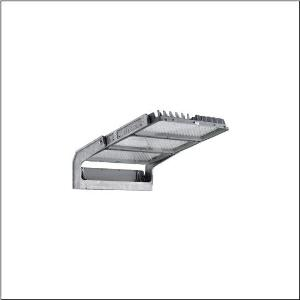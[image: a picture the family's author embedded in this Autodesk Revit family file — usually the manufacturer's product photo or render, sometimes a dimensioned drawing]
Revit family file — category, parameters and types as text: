
# Revit family: floodlight_fl_11_maxi_pro___rs07_5xa779124k01ab_afb2
name_source: partatom
category: Lighting Fixtures
units: mm (PartAtom-declared; Revit-internal decimal feet)

## family parameters
Cut with Voids When Loaded = No
Host = Face
Light Source = No
Part Type = Normal
Room Calculation Point = No
Round Connector Dimension = Use Diameter
Shared = No

## types (1)
- --- (1 x LED, 153810 lm, 1633.1 W, 5700K)
    Apparent Load = 1633 VA
    CIE Flux Codes = 80 93 99 100 99
    Color Rendering = 90
    Color Temperature = 5700K
    Default Elevation = 1800 mm
    Description = Floodlight FL 11  maxi  pro floodlight; light control with lens of PMMA; cover panel of toughened safety glass, transparent; light distribution: RS07, rotationally symmetric direct distribution, LED; colour temperature: 5700K, rated luminous flux: 153.810lm, colour rendering: CRI > 90, light colour: 957; luminous efficacy: 94lm/W; brightness control: DALI 2; with terminal, 5-pole, max. 2.5mm², mains connection: 220..240V/380..400V AC, 50/60Hz, surge voltage resistance: line to ground: 10kV, LED service life up to 100,000h L90. Typical operating time: 1000h per year., ECG replaceable separately, LED unit replaceable without ESD environment, dustproof LED module, dimming range 10..100%; 1633W floodlight with 3x LED unit of diecast aluminium, coated grey; length: 1.003mm / width: 651mm / height: 338mm; mounting bracket, of diecast aluminium, uncoated, natural, equipment: Power, protection rating (complete): IP66; insulation class (complete): insulation class I (protective earthing); certification: CE, ENEC, VDE; ball protection: ball impact resistant, only for outdoor installations in the designated locations, permissible operating ambient temperature: -40..+55°C, permissible storage temperature: -40..+85°Cpackaging unit: 1 piece

Light Distribution: RS07
    Height = 320 mm
    Lamp = 1 x LED
    Lamp Light Flux = 153810 lm
    Lamp Power = 1633.1 W
    Lamp count = 1
    Length = 1002 mm
    Luminous efficacy = 94 lm/W
    Manufacturer = Siteco
    ModVariant = No
    Model = 5XA779124K01AB
    Mounting Place = Ceiling
    Mounting Type = Surface mounted
    Number of Poles = 1
    OnlyDefault = Yes
    Power Factor = 1
    Product Name = Floodlight FL 11 maxi pro | RS07
    Product group = floodlight | ceiling mounted
    ProductGroupID = 303
    Protection Class = Protection class I
    Protection Degree = IP 66
    RLX_Detail_Level = 1
    RLX_Emergency_Light_Flux = 0 lm
    RLX_Emergency_Type = 0
    RLX_Emergency_Type_DB = No
    RlxData = <blob elided: 40393 chars, md5=3e690a37>
    Socket = socket
    Standby Power = 0 W
    System Light Flux = 153810 lm
    System Power = 1633 W
    Type Comments = factory setting: luminous flux: 100 % | dim-lin: 254 | 1100 mA
    Type Image = l_1356210.jpg
    URL = http://relux.com
    VarID = @adj_039137
    Voltage = 0 V
    Weight = 0.00 kg
    Width = 655 mm

## geometry (parser evidence)
native form markers: Blend x4, Sweep x12
no freeform markers — native parametric forms only
